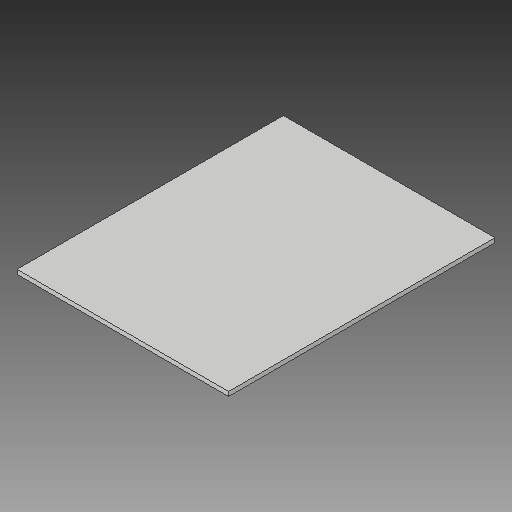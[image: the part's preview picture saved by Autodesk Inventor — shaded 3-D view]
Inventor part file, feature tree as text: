
AUTODESK INVENTOR PART (.ipt)
format: ipt  version: 2018.2 (Build 222227000, 227)  size: 79,872 bytes
history: native  units: in
note: dims shown in document units (in); Inventor stores cm internally (conversion verified against a paired STEP export)
features: other x3, reference x2, extrude x1, sketch x1
ambient origin geometry x8: Origin, YZ Plane, XZ Plane, XY Plane, X Axis, Y Axis, Z Axis, Center Point
bodies: Solid1 (feature_tree)
feature tree (7):
  extrude  "Extrusion1"  Depth=0.75in
  sketch  "Sketch1"  dims[d0=36.512in d1=0.75in d2=45.963in d3=0.0in]
  reference  "Reference1"
  reference  "Reference2"
  parser-record x1  (decoder bookkeeping rows leaked as tree rows — omitted from the tree; the rows remain in map.json)
  other  "Sax Cart.iam"
  other  "Wood Mount 1 Inch:5"
note: 1 file-system path scrubbed to <path> (originals preserved in map.json)
